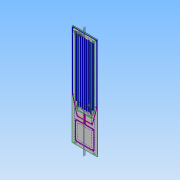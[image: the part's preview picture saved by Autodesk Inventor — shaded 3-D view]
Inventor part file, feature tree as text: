
AUTODESK INVENTOR PART (.ipt)
format: ipt  version: 2013 (Build 170138000, 138)  size: 399,872 bytes
history: native  units: in
note: dims shown in document units (in); Inventor stores cm internally (conversion verified against a paired STEP export)
features: other x15, extrude x3, hole x1, plane x1
ambient origin geometry x8: Origin, YZ Plane, XZ Plane, XY Plane, X Axis, Y Axis, Z Axis, Center Point
bodies: Solid1 (feature_tree)
feature tree (20):
  other  "Blocks"
  extrude  "Stock Extrusion"  Depth=23.8125in
  extrude  "Main rope pocket"  Depth=96.0in
  other  "Side profile reference"
  hole  "Hole1"  [1 undecoded]
  plane  "Work Plane1"
  extrude  "Through Panel Extrusion5"  Depth=58.0in
  other  "Exclaim Point"
  other  "Removal extra wood"
  other  "SignCenter"
  other  "Stock"
  other  "LEDPocket"
  other  "TwoLineColumn"
  other  "TwoLineColumnEnd"
  other  "15mm Neon profile"
  other  "U Bolt hole and bore"
  other  "U-Bolt holes"
  other  "WeatherProof panel"
  other  "15mm Neon profile:1"
  other  "15mm Neon profile:2"
note: 1 required parameter value undecoded (feature->parameter linkage not recoverable at this tier; creation-order binding heuristic only, values carry confidence <= 0.55)
